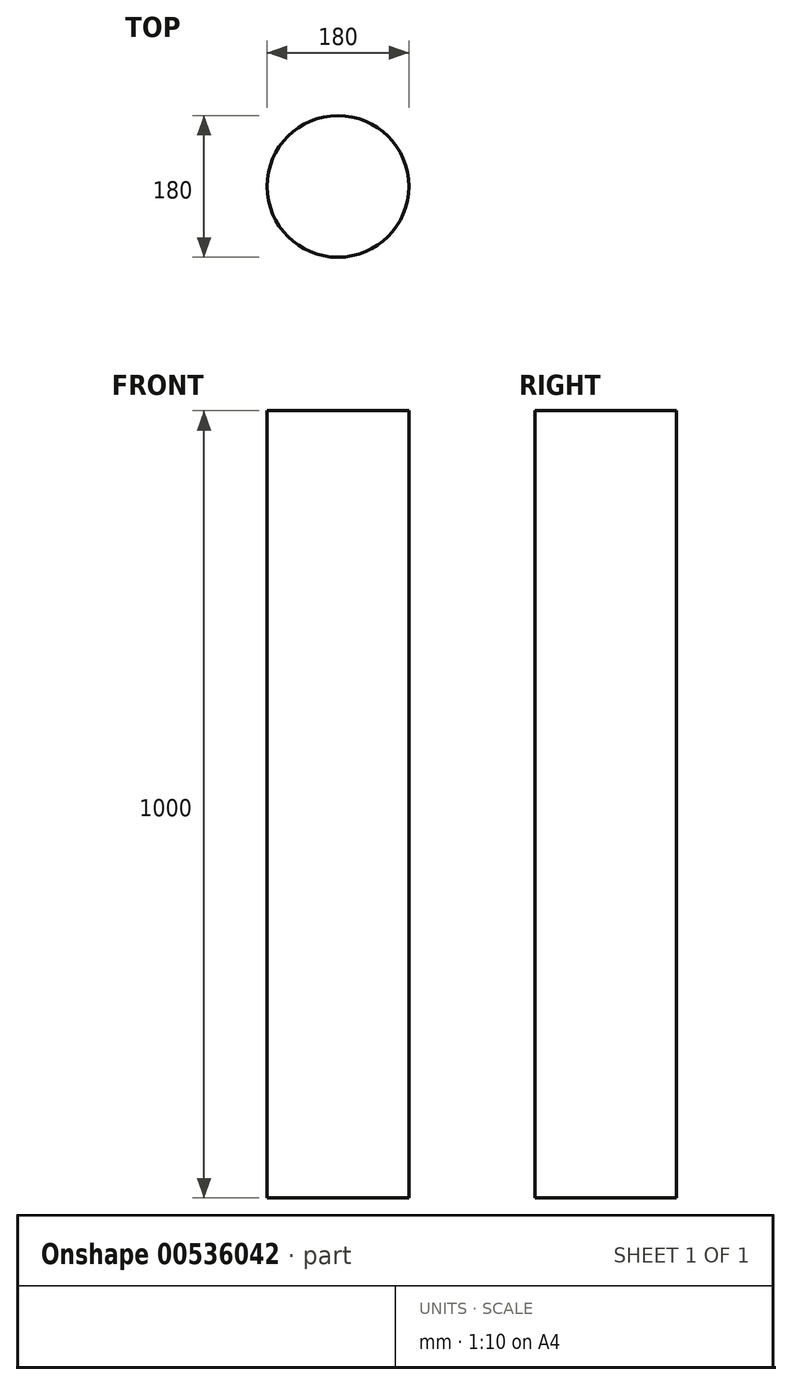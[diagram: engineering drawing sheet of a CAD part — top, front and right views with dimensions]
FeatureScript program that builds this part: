
annotation { "Feature Type Name" : "Feature", "Feature Type Description" : "" }
export const myFeature = defineFeature(function(context is Context, id is Id, definition is map)
    precondition{}
    {
        {
            var Q0;
            Q0=qCreatedBy(makeId("Top.planeOp"),FACE);
            var sketch = newSketch(context, id + "F0", { "sketchPlane" : qUnion([Q0])});
            skCircle(sketch, "E0", {"center": v(0, 0) * mm, "radius": 90 * mm});
            skSolve(sketch);
        }
        {
            var Q0;
            Q0 = qSketchRegion(id + "F0", true);
            extrude(context, id + "F1", {"entities" : qUnion([Q0]), "depth" : 1000 * mm, "offsetDistance" : 25 * mm});
        }
    });
